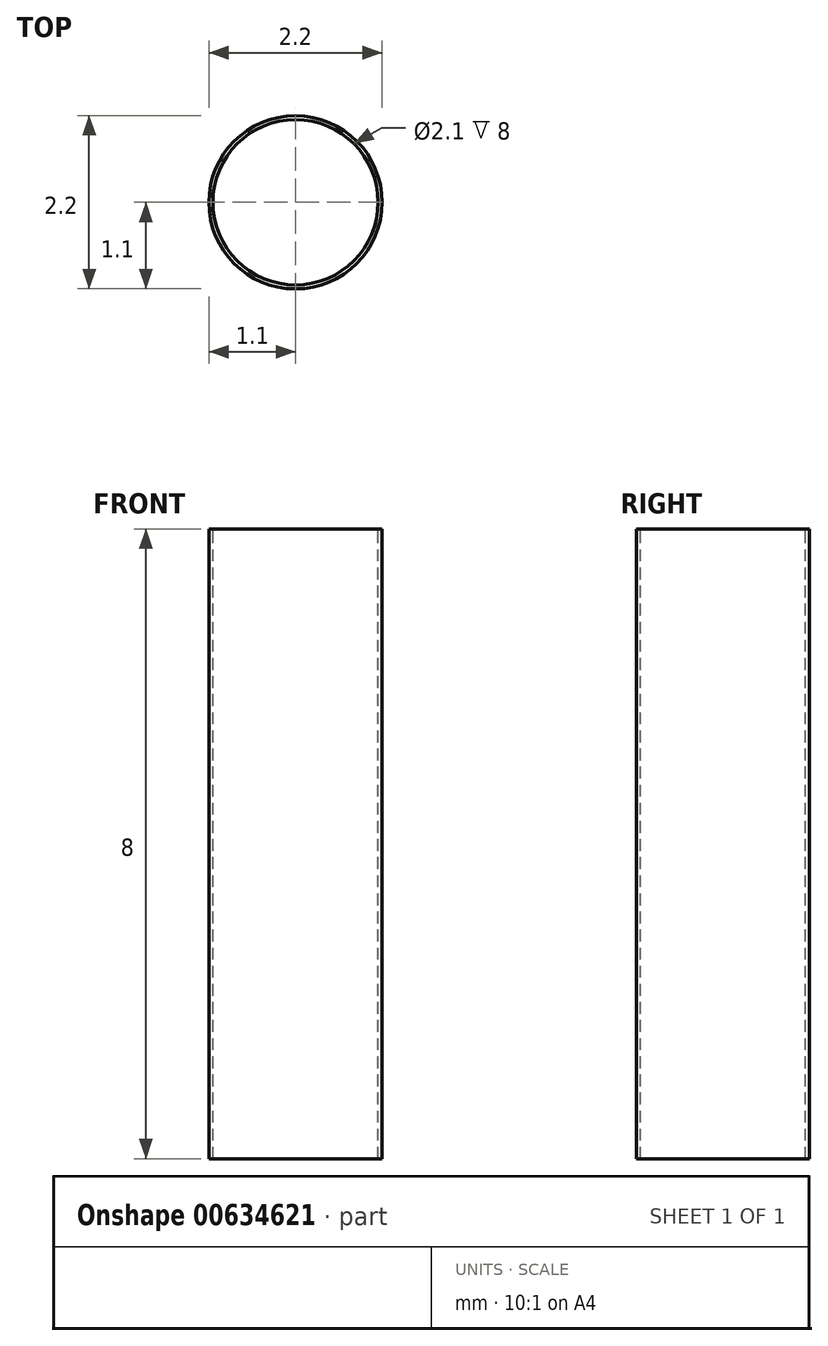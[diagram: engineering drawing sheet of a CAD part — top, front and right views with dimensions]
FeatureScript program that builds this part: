
annotation { "Feature Type Name" : "Feature", "Feature Type Description" : "" }
export const myFeature = defineFeature(function(context is Context, id is Id, definition is map)
    precondition{}
    {
        {
            var Q0;
            Q0=qCreatedBy(makeId("Top.planeOp"),FACE);
            var sketch = newSketch(context, id + "F0", { "sketchPlane" : qUnion([Q0])});
            skCircle(sketch, "E0", {"center": v(0, 0) * mm, "radius": 1.05 * mm});
            skCircle(sketch, "E1", {"center": v(0, 0) * mm, "radius": 1.1 * mm});
            skSolve(sketch);
        }
        {
            var Q0;
            Q0 = qSketchRegion(id + "F0", true);
            extrude(context, id + "F1", {"entities" : qUnion([Q0]), "oppositeDirection" : true, "depth" : 8 * mm, "offsetDistance" : 25 * mm});
        }
    });
